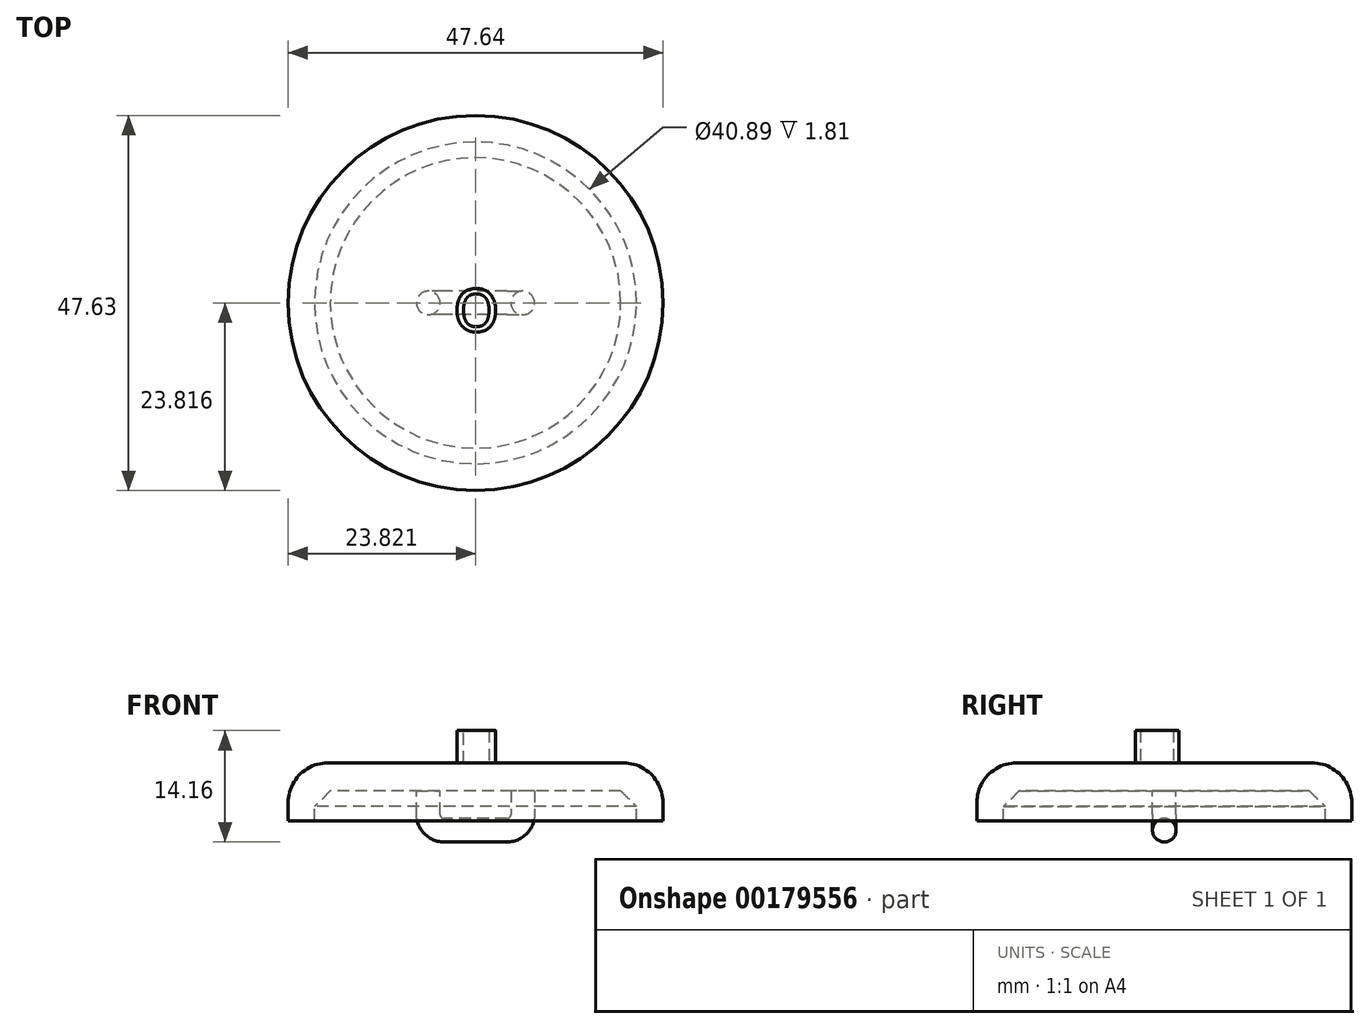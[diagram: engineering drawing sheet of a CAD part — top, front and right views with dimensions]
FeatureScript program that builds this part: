
annotation { "Feature Type Name" : "Feature", "Feature Type Description" : "" }
export const myFeature = defineFeature(function(context is Context, id is Id, definition is map)
    precondition{}
    {
        {
            var Q0;
            Q0=qCreatedBy(makeId("Top.planeOp"),FACE);
            var sketch = newSketch(context, id + "F0", { "sketchPlane" : qUnion([Q0])});
            skCircle(sketch, "E0", {"center": v(-110.65, 21.09) * mm, "radius": 23.82 * mm});
            skCircle(sketch, "E1", {"center": v(-110.65, 21.09) * mm, "radius": 20.45 * mm});
            skSolve(sketch);
        }
        {
            var Q0;
            Q0=makeQuery(id+"F0.imprint","IMPRINT",FACE,{"disambiguationData":[TD([[makeQuery(id+"F0.imprint","IMPRINT",EDGE,{"derivedFrom":sQuery(id+"F0.wireOp",EDGE,"E0")}),1.0]])]});
            extrude(context, id + "F1", {"entities" : qUnion([Q0]), "oppositeDirection" : true, "depth" : 3.8 * mm});
        }
        {
            var Q0;
            Q0=makeQuery(id+"F0.imprint","IMPRINT",FACE,{"disambiguationData":[TD([[makeQuery(id+"F0.imprint","IMPRINT",EDGE,{"derivedFrom":sQuery(id+"F0.wireOp",EDGE,"E1")}),1.0]])]});
            extrude(context, id + "F2", {"entities" : qUnion([Q0]), "depth" : 3.56 * mm});
        }
        {
            var Q0;
            Q0=makeQuery(id+"F0.imprint","IMPRINT",FACE,{"disambiguationData":[TD([[makeQuery(id+"F0.imprint","IMPRINT",EDGE,{"derivedFrom":sQuery(id+"F0.wireOp",EDGE,"E0")}),1.0]])]});
            extrude(context, id + "F3", {"entities" : qUnion([Q0]), "depth" : 3.56 * mm});
        }
        {
            var Q0;
            Q0=makeQuery(id+"F1.opExtrude","SWEPT_BODY",BODY,{"disambiguationData":[OSD([sQuery(id+"F0.wireOp",EDGE,"E0"),sQuery(id+"F0.wireOp",EDGE,"E1")])]});
            var Q1;
            Q1=makeQuery(id+"F2.opExtrude","SWEPT_BODY",BODY,{"disambiguationData":[OSD([sQuery(id+"F0.wireOp",EDGE,"E1")])]});
            var Q2;
            Q2=makeQuery(id+"F3.opExtrude","SWEPT_BODY",BODY,{"disambiguationData":[OSD([sQuery(id+"F0.wireOp",EDGE,"E0"),sQuery(id+"F0.wireOp",EDGE,"E1")])]});
            booleanBodies(context, id + "F4", {"operationType" : BooleanOperationType.UNION, "tools" : qUnion([Q0, Q1, Q2])});
        }
        {
            var Q0;
            Q0=makeQuery(id+"F3.opExtrude","CAP_EDGE",EDGE,{"disambiguationData":[OSD([sQuery(id+"F0.wireOp",EDGE,"E0")])],"isStart":false});
            fillet(context, id + "F5", {"entities" : qUnion([Q0]), "radius" : 5.08 * mm, "tangentPropagation" : true, "allowEdgeOverflow" : false});
        }
        {
            var Q0;
            Q0=makeQuery(id+"F1.opExtrude","CAP_EDGE",EDGE,{"disambiguationData":[OSD([sQuery(id+"F0.wireOp",EDGE,"E1")])],"isStart":true});
            chamfer(context, id + "F6", {"entities" : qUnion([Q0]), "width" : 2 * mm, "tangentPropagation" : true});
        }
        {
            var Q0;
            Q0=qCreatedBy(makeId("Front.planeOp"),FACE);
            var Q1;
            Q1=sQuery(id+"F0.wireOp",VERTEX,"E0.center");
            cPlane(context, id + "F7", {"entities" : qUnion([Q0, Q1]), "cplaneType" : CPlaneType.PLANE_POINT, "offset" : 25 * mm, "oppositeDirection" : true, "width" : 150 * mm, "height" : 150 * mm});
        }
        {
            var Q0;
            Q0=qCreatedBy(id+"F7.planeOp",FACE);
            var sketch = newSketch(context, id + "F8", { "sketchPlane" : qUnion([Q0])});
            skLineSegment(sketch, "E2.top", {"start": v(-106.65, -5) * mm, "end": v(-114.65, -5) * mm});
            skLineSegment(sketch, "E2.left", {"start": v(-104.65, 0) * mm, "end": v(-104.65, -3) * mm});
            skLineSegment(sketch, "E2.right", {"start": v(-116.65, 0) * mm, "end": v(-116.65, -3) * mm});
            skPoint(sketch, "E3.visualSharp", {"position": v(-104.65, -5) * mm});
            skArc(sketch, "E3.filletArc", {"start": v(-106.65, -5) * mm, "mid": v(-105.23, -4.41) * mm, "end": v(-104.65, -3) * mm});
            skPoint(sketch, "E4.visualSharp", {"position": v(-116.65, -5) * mm});
            skArc(sketch, "E4.filletArc", {"start": v(-116.65, -3) * mm, "mid": v(-116.06, -4.41) * mm, "end": v(-114.65, -5) * mm});
            skPoint(sketch, "E5.orphan", {"position": v(-131.1, 0) * mm});
            skPoint(sketch, "E6.orphan", {"position": v(-90.2, 0) * mm});
            skSolve(sketch);
        }
        {
            var Q0;
            Q0=makeQuery(id+"F0.imprint","IMPRINT",FACE,{"disambiguationData":[TD([[makeQuery(id+"F0.imprint","IMPRINT",EDGE,{"derivedFrom":sQuery(id+"F0.wireOp",EDGE,"E1")}),1.0]])]});
            var sketch = newSketch(context, id + "F9", { "sketchPlane" : qUnion([Q0])});
            skPoint(sketch, "E7.0", {"position": v(-104.65, 21.09) * mm});
            skCircle(sketch, "E8", {"center": v(-104.65, 21.09) * mm, "radius": 1.5 * mm});
            skSolve(sketch);
        }
        {
            var Q0;
            Q0=makeQuery(id+"F9.imprint","IMPRINT",FACE,{"disambiguationData":[TD([[makeQuery(id+"F9.imprint","IMPRINT",EDGE,{"derivedFrom":sQuery(id+"F9.wireOp",EDGE,"E8")}),1.0]])]});
            var Q1;
            Q1=sQuery(id+"F8.wireOp",EDGE,"E2.top");
            var Q2;
            Q2=sQuery(id+"F8.wireOp",EDGE,"E3.filletArc");
            var Q3;
            Q3=sQuery(id+"F8.wireOp",EDGE,"E2.left");
            var Q4;
            Q4=sQuery(id+"F8.wireOp",EDGE,"E4.filletArc");
            var Q5;
            Q5=sQuery(id+"F8.wireOp",EDGE,"E2.right");
            sweep(context, id + "F10", {"profiles" : qUnion([Q0]), "path" : qUnion([Q1, Q2, Q3, Q4, Q5])});
        }
        {
            var Q0;
            {var subQ0=sQuery(id+"F0.wireOp",EDGE,"E1");Q0=makeQuery(id+"F4.opBoolean","MERGE",FACE,{"derivedFrom":[makeQuery(id+"F2.opExtrude","CAP_FACE",FACE,{"disambiguationData":[OSD([subQ0])],"isStart":false}),makeQuery(id+"F3.opExtrude","CAP_FACE",FACE,{"disambiguationData":[OSD([sQuery(id+"F0.wireOp",EDGE,"E0"),subQ0])],"isStart":false})]});}
            var sketch = newSketch(context, id + "F11", { "sketchPlane" : qUnion([Q0])});
            skText(sketch, "E9", { "text": "lol", "fontName": "OpenSans-Regular.ttf"});
            skLineSegment(sketch, "E10", {"start": v(-116.1, 24.69) * mm, "end": v(-105.2, 17.48) * mm});
            skLineSegment(sketch, "E11", {"start": v(-105.2, 24.69) * mm, "end": v(-116.1, 17.48) * mm});
            skPoint(sketch, "E12", {"position": v(-110.65, 21.09) * mm});
            const initialGuessF11  = {"E9": [-0.1161, 0.01748, 1, 0, 0.0072]};
            skSetInitialGuess(sketch, initialGuessF11);
            skSolve(sketch);
        }
        {
            var Q0;
            {var subQ5=sQuery(id+"F11.wireOp",EDGE,"E9.sketch_text.stroke-11");var subQ6=sQuery(id+"F11.wireOp",EDGE,"E9.sketch_text.stroke-10");var subQ7=makeQuery(id+"F11.imprint","INTERSECT",VERTEX,{"derivedFrom":[subQ6,subQ5]});Q0=makeQuery(id+"F11.imprint","IMPRINT",FACE,{"disambiguationData":[TD([[makeQuery(id+"F11.imprint","IMPRINT",EDGE,{"disambiguationData":[TD([[subQ7,1.0]])],"derivedFrom":subQ6}),-1.0]])]});}
            var Q1;
            {var subQ0=sQuery(id+"F11.wireOp",EDGE,"E9.sketch_text.stroke-12");Q1=makeQuery(id+"F11.imprint","IMPRINT",FACE,{"disambiguationData":[TD([[makeQuery(id+"F11.imprint","IMPRINT",EDGE,{"derivedFrom":subQ0}),-1.0]])]});}
            var Q2;
            {var subQ13=sQuery(id+"F11.wireOp",EDGE,"E9.sketch_text.stroke-5");Q2=makeQuery(id+"F11.imprint","IMPRINT",FACE,{"disambiguationData":[TD([[makeQuery(id+"F11.imprint","IMPRINT",EDGE,{"derivedFrom":subQ13}),-1.0]])]});}
            var Q3;
            {var subQ5=sQuery(id+"F11.wireOp",EDGE,"E9.sketch_text.stroke-9");Q3=makeQuery(id+"F11.imprint","IMPRINT",FACE,{"disambiguationData":[TD([[makeQuery(id+"F11.imprint","IMPRINT",EDGE,{"derivedFrom":subQ5}),-1.0]])]});}
            extrude(context, id + "F12", {"entities" : qUnion([Q0, Q1, Q2, Q3]), "operationType" : NewBodyOperationType.ADD, "depth" : 4.1 * mm});
        }
    });
